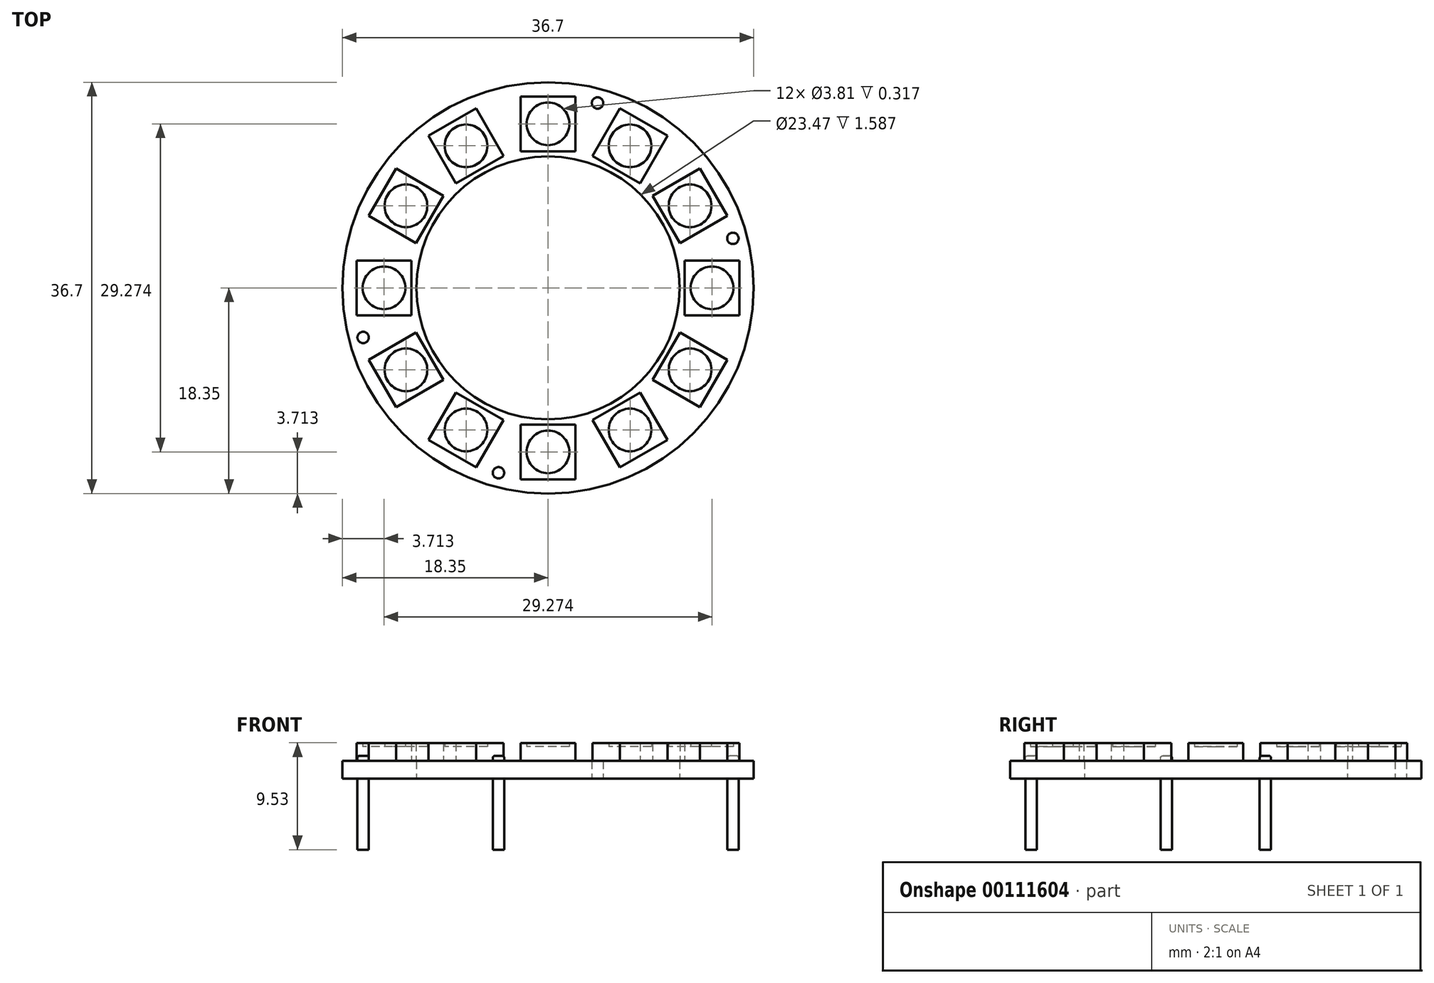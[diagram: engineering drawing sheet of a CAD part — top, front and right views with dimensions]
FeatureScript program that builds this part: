
annotation { "Feature Type Name" : "Feature", "Feature Type Description" : "" }
export const myFeature = defineFeature(function(context is Context, id is Id, definition is map)
    precondition{}
    {
        {
            var Q0;
            Q0=qCreatedBy(makeId("Top.planeOp"),FACE);
            var sketch = newSketch(context, id + "F0", { "sketchPlane" : qUnion([Q0])});
            skCircle(sketch, "E0", {"center": v(0, 0) * mm, "radius": 18.35 * mm});
            skCircle(sketch, "E1", {"center": v(0, 0) * mm, "radius": 11.73 * mm});
            skLineSegment(sketch, "E2", {"start": v(0, 0) * mm, "end": v(0, 18.35) * mm, "construction": true});
            skLineSegment(sketch, "E3.1.0", {"start": v(0, 0) * mm, "end": v(-4.75, 17.73) * mm, "construction": true});
            skLineSegment(sketch, "E3.2.0", {"start": v(0, 0) * mm, "end": v(-9.18, 15.9) * mm, "construction": true});
            skLineSegment(sketch, "E3.3.0", {"start": v(0, 0) * mm, "end": v(-12.98, 12.98) * mm, "construction": true});
            skLineSegment(sketch, "E3.4.0", {"start": v(0, 0) * mm, "end": v(-15.9, 9.18) * mm, "construction": true});
            skLineSegment(sketch, "E3.5.0", {"start": v(0, 0) * mm, "end": v(-17.73, 4.75) * mm, "construction": true});
            skLineSegment(sketch, "E3.6.0", {"start": v(0, 0) * mm, "end": v(-18.35, 0) * mm, "construction": true});
            skLineSegment(sketch, "E3.7.0", {"start": v(0, 0) * mm, "end": v(-17.73, -4.75) * mm, "construction": true});
            skLineSegment(sketch, "E3.8.0", {"start": v(0, 0) * mm, "end": v(-15.9, -9.18) * mm, "construction": true});
            skLineSegment(sketch, "E3.9.0", {"start": v(0, 0) * mm, "end": v(-12.98, -12.98) * mm, "construction": true});
            skLineSegment(sketch, "E3.10.0", {"start": v(0, 0) * mm, "end": v(-9.18, -15.9) * mm, "construction": true});
            skLineSegment(sketch, "E3.11.0", {"start": v(0, 0) * mm, "end": v(-4.75, -17.73) * mm, "construction": true});
            skLineSegment(sketch, "E3.12.0", {"start": v(0, 0) * mm, "end": v(0, -18.35) * mm, "construction": true});
            skLineSegment(sketch, "E3.13.0", {"start": v(0, 0) * mm, "end": v(4.75, -17.73) * mm, "construction": true});
            skLineSegment(sketch, "E3.14.0", {"start": v(0, 0) * mm, "end": v(9.18, -15.9) * mm, "construction": true});
            skLineSegment(sketch, "E3.15.0", {"start": v(0, 0) * mm, "end": v(12.98, -12.98) * mm, "construction": true});
            skLineSegment(sketch, "E3.16.0", {"start": v(0, 0) * mm, "end": v(15.9, -9.18) * mm, "construction": true});
            skLineSegment(sketch, "E3.17.0", {"start": v(0, 0) * mm, "end": v(17.73, -4.75) * mm, "construction": true});
            skLineSegment(sketch, "E3.18.0", {"start": v(0, 0) * mm, "end": v(18.35, 0) * mm, "construction": true});
            skLineSegment(sketch, "E3.19.0", {"start": v(0, 0) * mm, "end": v(17.73, 4.75) * mm, "construction": true});
            skLineSegment(sketch, "E3.20.0", {"start": v(0, 0) * mm, "end": v(15.9, 9.18) * mm, "construction": true});
            skLineSegment(sketch, "E3.21.0", {"start": v(0, 0) * mm, "end": v(12.98, 12.98) * mm, "construction": true});
            skLineSegment(sketch, "E3.22.0", {"start": v(0, 0) * mm, "end": v(9.18, 15.9) * mm, "construction": true});
            skLineSegment(sketch, "E3.23.0", {"start": v(0, 0) * mm, "end": v(4.75, 17.73) * mm, "construction": true});
            skCircle(sketch, "E4", {"center": v(4.42, 16.5) * mm, "radius": 0.5 * mm});
            skCircle(sketch, "E5", {"center": v(16.5, 4.42) * mm, "radius": 0.5 * mm});
            skCircle(sketch, "E6", {"center": v(-16.5, -4.42) * mm, "radius": 0.5 * mm});
            skCircle(sketch, "E7", {"center": v(-4.42, -16.5) * mm, "radius": 0.5 * mm});
            skSolve(sketch);
        }
        {
            var Q0;
            Q0=makeQuery(id+"F0.imprint","IMPRINT",FACE,{"disambiguationData":[TD([[makeQuery(id+"F0.imprint","IMPRINT",EDGE,{"derivedFrom":sQuery(id+"F0.wireOp",EDGE,"E0")}),1.0]])]});
            extrude(context, id + "F1", {"entities" : qUnion([Q0]), "depth" : 1.59 * mm});
        }
        {
            var Q0;
            Q0=makeQuery(id+"F1.opExtrude","CAP_FACE",FACE,{"disambiguationData":[OSD([sQuery(id+"F0.wireOp",EDGE,"E0"),sQuery(id+"F0.wireOp",EDGE,"E1"),sQuery(id+"F0.wireOp",EDGE,"E4"),sQuery(id+"F0.wireOp",EDGE,"E5"),sQuery(id+"F0.wireOp",EDGE,"E6"),sQuery(id+"F0.wireOp",EDGE,"E7")])],"isStart":false});
            var sketch = newSketch(context, id + "F2", { "sketchPlane" : qUnion([Q0])});
            skLineSegment(sketch, "E8.bottom", {"start": v(-2.44, 17.08) * mm, "end": v(2.44, 17.08) * mm});
            skLineSegment(sketch, "E8.top", {"start": v(-2.44, 12.2) * mm, "end": v(2.44, 12.2) * mm});
            skLineSegment(sketch, "E8.left", {"start": v(-2.44, 17.08) * mm, "end": v(-2.44, 12.2) * mm});
            skLineSegment(sketch, "E8.right", {"start": v(2.44, 17.08) * mm, "end": v(2.44, 12.2) * mm});
            skCircle(sketch, "E9", {"center": v(0, 14.64) * mm, "radius": 1.9 * mm});
            skPoint(sketch, "E9.centerSnap0", {"position": v(-2.44, 14.64) * mm});
            skCircle(sketch, "E10.1.0", {"center": v(-7.32, 12.68) * mm, "radius": 1.9 * mm});
            skLineSegment(sketch, "E10.1.1", {"start": v(-10.66, 13.57) * mm, "end": v(-6.42, 16.02) * mm});
            skLineSegment(sketch, "E10.1.2", {"start": v(-6.42, 16.02) * mm, "end": v(-3.98, 11.78) * mm});
            skLineSegment(sketch, "E10.1.3", {"start": v(-8.21, 9.34) * mm, "end": v(-3.98, 11.78) * mm});
            skLineSegment(sketch, "E10.1.4", {"start": v(-10.66, 13.57) * mm, "end": v(-8.21, 9.34) * mm});
            skCircle(sketch, "E10.2.0", {"center": v(-12.68, 7.32) * mm, "radius": 1.9 * mm});
            skLineSegment(sketch, "E10.2.1", {"start": v(-16.02, 6.42) * mm, "end": v(-13.57, 10.66) * mm});
            skLineSegment(sketch, "E10.2.2", {"start": v(-13.57, 10.66) * mm, "end": v(-9.34, 8.21) * mm});
            skLineSegment(sketch, "E10.2.3", {"start": v(-11.78, 3.98) * mm, "end": v(-9.34, 8.21) * mm});
            skLineSegment(sketch, "E10.2.4", {"start": v(-16.02, 6.42) * mm, "end": v(-11.78, 3.98) * mm});
            skCircle(sketch, "E10.3.0", {"center": v(-14.64, 0) * mm, "radius": 1.9 * mm});
            skLineSegment(sketch, "E10.3.1", {"start": v(-17.08, -2.44) * mm, "end": v(-17.08, 2.44) * mm});
            skLineSegment(sketch, "E10.3.2", {"start": v(-17.08, 2.44) * mm, "end": v(-12.2, 2.44) * mm});
            skLineSegment(sketch, "E10.3.3", {"start": v(-12.2, -2.44) * mm, "end": v(-12.2, 2.44) * mm});
            skLineSegment(sketch, "E10.3.4", {"start": v(-17.08, -2.44) * mm, "end": v(-12.2, -2.44) * mm});
            skCircle(sketch, "E10.4.0", {"center": v(-12.68, -7.32) * mm, "radius": 1.9 * mm});
            skLineSegment(sketch, "E10.4.1", {"start": v(-13.57, -10.66) * mm, "end": v(-16.02, -6.42) * mm});
            skLineSegment(sketch, "E10.4.2", {"start": v(-16.02, -6.42) * mm, "end": v(-11.78, -3.98) * mm});
            skLineSegment(sketch, "E10.4.3", {"start": v(-9.34, -8.21) * mm, "end": v(-11.78, -3.98) * mm});
            skLineSegment(sketch, "E10.4.4", {"start": v(-13.57, -10.66) * mm, "end": v(-9.34, -8.21) * mm});
            skCircle(sketch, "E10.5.0", {"center": v(-7.32, -12.68) * mm, "radius": 1.9 * mm});
            skLineSegment(sketch, "E10.5.1", {"start": v(-6.42, -16.02) * mm, "end": v(-10.66, -13.57) * mm});
            skLineSegment(sketch, "E10.5.2", {"start": v(-10.66, -13.57) * mm, "end": v(-8.21, -9.34) * mm});
            skLineSegment(sketch, "E10.5.3", {"start": v(-3.98, -11.78) * mm, "end": v(-8.21, -9.34) * mm});
            skLineSegment(sketch, "E10.5.4", {"start": v(-6.42, -16.02) * mm, "end": v(-3.98, -11.78) * mm});
            skCircle(sketch, "E10.6.0", {"center": v(0, -14.64) * mm, "radius": 1.9 * mm});
            skLineSegment(sketch, "E10.6.1", {"start": v(2.44, -17.08) * mm, "end": v(-2.44, -17.08) * mm});
            skLineSegment(sketch, "E10.6.2", {"start": v(-2.44, -17.08) * mm, "end": v(-2.44, -12.2) * mm});
            skLineSegment(sketch, "E10.6.3", {"start": v(2.44, -12.2) * mm, "end": v(-2.44, -12.2) * mm});
            skLineSegment(sketch, "E10.6.4", {"start": v(2.44, -17.08) * mm, "end": v(2.44, -12.2) * mm});
            skCircle(sketch, "E10.7.0", {"center": v(7.32, -12.68) * mm, "radius": 1.9 * mm});
            skLineSegment(sketch, "E10.7.1", {"start": v(10.66, -13.57) * mm, "end": v(6.42, -16.02) * mm});
            skLineSegment(sketch, "E10.7.2", {"start": v(6.42, -16.02) * mm, "end": v(3.98, -11.78) * mm});
            skLineSegment(sketch, "E10.7.3", {"start": v(8.21, -9.34) * mm, "end": v(3.98, -11.78) * mm});
            skLineSegment(sketch, "E10.7.4", {"start": v(10.66, -13.57) * mm, "end": v(8.21, -9.34) * mm});
            skCircle(sketch, "E10.8.0", {"center": v(12.68, -7.32) * mm, "radius": 1.9 * mm});
            skLineSegment(sketch, "E10.8.1", {"start": v(16.02, -6.42) * mm, "end": v(13.57, -10.66) * mm});
            skLineSegment(sketch, "E10.8.2", {"start": v(13.57, -10.66) * mm, "end": v(9.34, -8.21) * mm});
            skLineSegment(sketch, "E10.8.3", {"start": v(11.78, -3.98) * mm, "end": v(9.34, -8.21) * mm});
            skLineSegment(sketch, "E10.8.4", {"start": v(16.02, -6.42) * mm, "end": v(11.78, -3.98) * mm});
            skCircle(sketch, "E10.9.0", {"center": v(14.64, 0) * mm, "radius": 1.9 * mm});
            skLineSegment(sketch, "E10.9.1", {"start": v(17.08, 2.44) * mm, "end": v(17.08, -2.44) * mm});
            skLineSegment(sketch, "E10.9.2", {"start": v(17.08, -2.44) * mm, "end": v(12.2, -2.44) * mm});
            skLineSegment(sketch, "E10.9.3", {"start": v(12.2, 2.44) * mm, "end": v(12.2, -2.44) * mm});
            skLineSegment(sketch, "E10.9.4", {"start": v(17.08, 2.44) * mm, "end": v(12.2, 2.44) * mm});
            skCircle(sketch, "E10.10.0", {"center": v(12.68, 7.32) * mm, "radius": 1.9 * mm});
            skLineSegment(sketch, "E10.10.1", {"start": v(13.57, 10.66) * mm, "end": v(16.02, 6.42) * mm});
            skLineSegment(sketch, "E10.10.2", {"start": v(16.02, 6.42) * mm, "end": v(11.78, 3.98) * mm});
            skLineSegment(sketch, "E10.10.3", {"start": v(9.34, 8.21) * mm, "end": v(11.78, 3.98) * mm});
            skLineSegment(sketch, "E10.10.4", {"start": v(13.57, 10.66) * mm, "end": v(9.34, 8.21) * mm});
            skCircle(sketch, "E10.11.0", {"center": v(7.32, 12.68) * mm, "radius": 1.9 * mm});
            skLineSegment(sketch, "E10.11.1", {"start": v(6.42, 16.02) * mm, "end": v(10.66, 13.57) * mm});
            skLineSegment(sketch, "E10.11.2", {"start": v(10.66, 13.57) * mm, "end": v(8.21, 9.34) * mm});
            skLineSegment(sketch, "E10.11.3", {"start": v(3.98, 11.78) * mm, "end": v(8.21, 9.34) * mm});
            skLineSegment(sketch, "E10.11.4", {"start": v(6.42, 16.02) * mm, "end": v(3.98, 11.78) * mm});
            skPoint(sketch, "E10.center", {"position": v(0, 0) * mm});
            skSolve(sketch);
        }
        {
            var Q0;
            Q0 = qSketchRegion(id + "F2", true);
            extrude(context, id + "F3", {"entities" : qUnion([Q0]), "operationType" : NewBodyOperationType.ADD, "depth" : 1.59 * mm});
        }
        {
            var Q0;
            Q0=makeQuery(id+"F3.boolean.opBoolean","SPLIT",FACE,{"disambiguationData":[TD([makeQuery(id+"F3.opExtrude","SWEPT_FACE",FACE,{"disambiguationData":[OSD([sQuery(id+"F2.wireOp",EDGE,"E9")])]})])],"derivedFrom":makeQuery(id+"F1.opExtrude","CAP_FACE",FACE,{"disambiguationData":[OSD([sQuery(id+"F0.wireOp",EDGE,"E0"),sQuery(id+"F0.wireOp",EDGE,"E1"),sQuery(id+"F0.wireOp",EDGE,"E4"),sQuery(id+"F0.wireOp",EDGE,"E5"),sQuery(id+"F0.wireOp",EDGE,"E6"),sQuery(id+"F0.wireOp",EDGE,"E7")])],"isStart":false})});
            var Q1;
            Q1=makeQuery(id+"F3.boolean.opBoolean","SPLIT",FACE,{"disambiguationData":[TD([makeQuery(id+"F3.opExtrude","SWEPT_FACE",FACE,{"disambiguationData":[OSD([sQuery(id+"F2.wireOp",EDGE,"E10.11.0")])]})])],"derivedFrom":makeQuery(id+"F1.opExtrude","CAP_FACE",FACE,{"disambiguationData":[OSD([sQuery(id+"F0.wireOp",EDGE,"E0"),sQuery(id+"F0.wireOp",EDGE,"E1"),sQuery(id+"F0.wireOp",EDGE,"E4"),sQuery(id+"F0.wireOp",EDGE,"E5"),sQuery(id+"F0.wireOp",EDGE,"E6"),sQuery(id+"F0.wireOp",EDGE,"E7")])],"isStart":false})});
            var Q2;
            Q2=makeQuery(id+"F3.boolean.opBoolean","SPLIT",FACE,{"disambiguationData":[TD([makeQuery(id+"F3.opExtrude","SWEPT_FACE",FACE,{"disambiguationData":[OSD([sQuery(id+"F2.wireOp",EDGE,"E10.10.0")])]})])],"derivedFrom":makeQuery(id+"F1.opExtrude","CAP_FACE",FACE,{"disambiguationData":[OSD([sQuery(id+"F0.wireOp",EDGE,"E0"),sQuery(id+"F0.wireOp",EDGE,"E1"),sQuery(id+"F0.wireOp",EDGE,"E4"),sQuery(id+"F0.wireOp",EDGE,"E5"),sQuery(id+"F0.wireOp",EDGE,"E6"),sQuery(id+"F0.wireOp",EDGE,"E7")])],"isStart":false})});
            var Q3;
            Q3=makeQuery(id+"F3.boolean.opBoolean","SPLIT",FACE,{"disambiguationData":[TD([makeQuery(id+"F3.opExtrude","SWEPT_FACE",FACE,{"disambiguationData":[OSD([sQuery(id+"F2.wireOp",EDGE,"E10.9.0")])]})])],"derivedFrom":makeQuery(id+"F1.opExtrude","CAP_FACE",FACE,{"disambiguationData":[OSD([sQuery(id+"F0.wireOp",EDGE,"E0"),sQuery(id+"F0.wireOp",EDGE,"E1"),sQuery(id+"F0.wireOp",EDGE,"E4"),sQuery(id+"F0.wireOp",EDGE,"E5"),sQuery(id+"F0.wireOp",EDGE,"E6"),sQuery(id+"F0.wireOp",EDGE,"E7")])],"isStart":false})});
            var Q4;
            Q4=makeQuery(id+"F3.boolean.opBoolean","SPLIT",FACE,{"disambiguationData":[TD([makeQuery(id+"F3.opExtrude","SWEPT_FACE",FACE,{"disambiguationData":[OSD([sQuery(id+"F2.wireOp",EDGE,"E10.8.0")])]})])],"derivedFrom":makeQuery(id+"F1.opExtrude","CAP_FACE",FACE,{"disambiguationData":[OSD([sQuery(id+"F0.wireOp",EDGE,"E0"),sQuery(id+"F0.wireOp",EDGE,"E1"),sQuery(id+"F0.wireOp",EDGE,"E4"),sQuery(id+"F0.wireOp",EDGE,"E5"),sQuery(id+"F0.wireOp",EDGE,"E6"),sQuery(id+"F0.wireOp",EDGE,"E7")])],"isStart":false})});
            var Q5;
            Q5=makeQuery(id+"F3.boolean.opBoolean","SPLIT",FACE,{"disambiguationData":[TD([makeQuery(id+"F3.opExtrude","SWEPT_FACE",FACE,{"disambiguationData":[OSD([sQuery(id+"F2.wireOp",EDGE,"E10.7.0")])]})])],"derivedFrom":makeQuery(id+"F1.opExtrude","CAP_FACE",FACE,{"disambiguationData":[OSD([sQuery(id+"F0.wireOp",EDGE,"E0"),sQuery(id+"F0.wireOp",EDGE,"E1"),sQuery(id+"F0.wireOp",EDGE,"E4"),sQuery(id+"F0.wireOp",EDGE,"E5"),sQuery(id+"F0.wireOp",EDGE,"E6"),sQuery(id+"F0.wireOp",EDGE,"E7")])],"isStart":false})});
            var Q6;
            Q6=makeQuery(id+"F3.boolean.opBoolean","SPLIT",FACE,{"disambiguationData":[TD([makeQuery(id+"F3.opExtrude","SWEPT_FACE",FACE,{"disambiguationData":[OSD([sQuery(id+"F2.wireOp",EDGE,"E10.6.0")])]})])],"derivedFrom":makeQuery(id+"F1.opExtrude","CAP_FACE",FACE,{"disambiguationData":[OSD([sQuery(id+"F0.wireOp",EDGE,"E0"),sQuery(id+"F0.wireOp",EDGE,"E1"),sQuery(id+"F0.wireOp",EDGE,"E4"),sQuery(id+"F0.wireOp",EDGE,"E5"),sQuery(id+"F0.wireOp",EDGE,"E6"),sQuery(id+"F0.wireOp",EDGE,"E7")])],"isStart":false})});
            var Q7;
            Q7=makeQuery(id+"F3.boolean.opBoolean","SPLIT",FACE,{"disambiguationData":[TD([makeQuery(id+"F3.opExtrude","SWEPT_FACE",FACE,{"disambiguationData":[OSD([sQuery(id+"F2.wireOp",EDGE,"E10.5.0")])]})])],"derivedFrom":makeQuery(id+"F1.opExtrude","CAP_FACE",FACE,{"disambiguationData":[OSD([sQuery(id+"F0.wireOp",EDGE,"E0"),sQuery(id+"F0.wireOp",EDGE,"E1"),sQuery(id+"F0.wireOp",EDGE,"E4"),sQuery(id+"F0.wireOp",EDGE,"E5"),sQuery(id+"F0.wireOp",EDGE,"E6"),sQuery(id+"F0.wireOp",EDGE,"E7")])],"isStart":false})});
            var Q8;
            Q8=makeQuery(id+"F3.boolean.opBoolean","SPLIT",FACE,{"disambiguationData":[TD([makeQuery(id+"F3.opExtrude","SWEPT_FACE",FACE,{"disambiguationData":[OSD([sQuery(id+"F2.wireOp",EDGE,"E10.4.0")])]})])],"derivedFrom":makeQuery(id+"F1.opExtrude","CAP_FACE",FACE,{"disambiguationData":[OSD([sQuery(id+"F0.wireOp",EDGE,"E0"),sQuery(id+"F0.wireOp",EDGE,"E1"),sQuery(id+"F0.wireOp",EDGE,"E4"),sQuery(id+"F0.wireOp",EDGE,"E5"),sQuery(id+"F0.wireOp",EDGE,"E6"),sQuery(id+"F0.wireOp",EDGE,"E7")])],"isStart":false})});
            var Q9;
            Q9=makeQuery(id+"F3.boolean.opBoolean","SPLIT",FACE,{"disambiguationData":[TD([makeQuery(id+"F3.opExtrude","SWEPT_FACE",FACE,{"disambiguationData":[OSD([sQuery(id+"F2.wireOp",EDGE,"E10.3.0")])]})])],"derivedFrom":makeQuery(id+"F1.opExtrude","CAP_FACE",FACE,{"disambiguationData":[OSD([sQuery(id+"F0.wireOp",EDGE,"E0"),sQuery(id+"F0.wireOp",EDGE,"E1"),sQuery(id+"F0.wireOp",EDGE,"E4"),sQuery(id+"F0.wireOp",EDGE,"E5"),sQuery(id+"F0.wireOp",EDGE,"E6"),sQuery(id+"F0.wireOp",EDGE,"E7")])],"isStart":false})});
            var Q10;
            Q10=makeQuery(id+"F3.boolean.opBoolean","SPLIT",FACE,{"disambiguationData":[TD([makeQuery(id+"F3.opExtrude","SWEPT_FACE",FACE,{"disambiguationData":[OSD([sQuery(id+"F2.wireOp",EDGE,"E10.2.0")])]})])],"derivedFrom":makeQuery(id+"F1.opExtrude","CAP_FACE",FACE,{"disambiguationData":[OSD([sQuery(id+"F0.wireOp",EDGE,"E0"),sQuery(id+"F0.wireOp",EDGE,"E1"),sQuery(id+"F0.wireOp",EDGE,"E4"),sQuery(id+"F0.wireOp",EDGE,"E5"),sQuery(id+"F0.wireOp",EDGE,"E6"),sQuery(id+"F0.wireOp",EDGE,"E7")])],"isStart":false})});
            var Q11;
            Q11=makeQuery(id+"F3.boolean.opBoolean","SPLIT",FACE,{"disambiguationData":[TD([makeQuery(id+"F3.opExtrude","SWEPT_FACE",FACE,{"disambiguationData":[OSD([sQuery(id+"F2.wireOp",EDGE,"E10.1.0")])]})])],"derivedFrom":makeQuery(id+"F1.opExtrude","CAP_FACE",FACE,{"disambiguationData":[OSD([sQuery(id+"F0.wireOp",EDGE,"E0"),sQuery(id+"F0.wireOp",EDGE,"E1"),sQuery(id+"F0.wireOp",EDGE,"E4"),sQuery(id+"F0.wireOp",EDGE,"E5"),sQuery(id+"F0.wireOp",EDGE,"E6"),sQuery(id+"F0.wireOp",EDGE,"E7")])],"isStart":false})});
            extrude(context, id + "F4", {"entities" : qUnion([Q0, Q1, Q2, Q3, Q4, Q5, Q6, Q7, Q8, Q9, Q10, Q11]), "operationType" : NewBodyOperationType.ADD, "depth" : 1.27 * mm});
        }
        {
            var Q0;
            Q0=makeQuery(id+"F0.imprint","IMPRINT",FACE,{"disambiguationData":[TD([[makeQuery(id+"F0.imprint","IMPRINT",EDGE,{"derivedFrom":sQuery(id+"F0.wireOp",EDGE,"E7")}),1.0]])]});
            var Q1;
            Q1=makeQuery(id+"F0.imprint","IMPRINT",FACE,{"disambiguationData":[TD([[makeQuery(id+"F0.imprint","IMPRINT",EDGE,{"derivedFrom":sQuery(id+"F0.wireOp",EDGE,"E6")}),1.0]])]});
            var Q2;
            Q2=makeQuery(id+"F0.imprint","IMPRINT",FACE,{"disambiguationData":[TD([[makeQuery(id+"F0.imprint","IMPRINT",EDGE,{"derivedFrom":sQuery(id+"F0.wireOp",EDGE,"E5")}),1.0]])]});
            extrude(context, id + "F5", {"entities" : qUnion([Q0, Q1, Q2]), "operationType" : NewBodyOperationType.ADD, "oppositeDirection" : true, "depth" : 6.35 * mm, "hasSecondDirection" : true, "secondDirectionOppositeDirection" : false, "secondDirectionDepth" : 2.03 * mm});
        }
        {
            var Q0;
            Q0=makeQuery(id+"F1.opExtrude","CAP_EDGE",EDGE,{"disambiguationData":[OSD([sQuery(id+"F0.wireOp",EDGE,"E5")])],"isStart":false});
            var Q1;
            Q1=makeQuery(id+"F5.opExtrude","CAP_EDGE",EDGE,{"disambiguationData":[OSD([sQuery(id+"F0.wireOp",EDGE,"E5")])],"isStart":true});
            var Q2;
            Q2=makeQuery(id+"F5.opExtrude","CAP_EDGE",EDGE,{"disambiguationData":[OSD([sQuery(id+"F0.wireOp",EDGE,"E6")])],"isStart":true});
            var Q3;
            Q3=makeQuery(id+"F5.opExtrude","CAP_EDGE",EDGE,{"disambiguationData":[OSD([sQuery(id+"F0.wireOp",EDGE,"E7")])],"isStart":true});
            var Q4;
            Q4=makeQuery(id+"F1.opExtrude","CAP_EDGE",EDGE,{"disambiguationData":[OSD([sQuery(id+"F0.wireOp",EDGE,"E6")])],"isStart":false});
            var Q5;
            Q5=makeQuery(id+"F1.opExtrude","CAP_EDGE",EDGE,{"disambiguationData":[OSD([sQuery(id+"F0.wireOp",EDGE,"E7")])],"isStart":false});
            fillet(context, id + "F6", {"entities" : qUnion([Q0, Q1, Q2, Q3, Q4, Q5]), "radius" : 0.2 * mm, "tangentPropagation" : true, "allowEdgeOverflow" : false});
        }
    });
